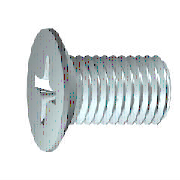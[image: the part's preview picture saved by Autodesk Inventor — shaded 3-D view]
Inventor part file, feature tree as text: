
AUTODESK INVENTOR PART (.ipt)
format: ipt  version: 2022 (Build 260153000, 153)  size: 230,912 bytes
history: native  units: mm (DEFAULTED — no unit token found)
features: sketch x1, extrude x1, plane x1
ambient origin geometry x7: Origin, YZ Plane, XZ Plane, X Axis, Y Axis, Z Axis, Center Point
bodies: Solid1 (feature_tree), Body (feature_tree)
feature tree (3):
  sketch  "Sketch1"  dims[d0=25.4mm d1=1.524mm d2=3.5052mm d3=6.0452mm d8=90.0deg d4=2.1844mm d5=3.9116mm d6=4.625123mm d7=10.821041mm d9=19.05mm d10=0.0mm d11=0.472281mm d12=0.472281mm d13=8.726646mm d14=1.524mm d15=50.8mm d45=2.1844mm d16=0.0mm d17=3.9116mm d18=45.0deg d19=1.303867mm d20=1.9558mm d21=3.9116mm d22=0.3429mm d24=0.0mm d25=0.13716mm d62=45.0deg d65=0.0mm d66=0.0mm]
  extrude  "Slot"  Depth=0.13716mm
  plane  "Work Plane2"
